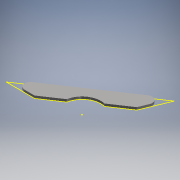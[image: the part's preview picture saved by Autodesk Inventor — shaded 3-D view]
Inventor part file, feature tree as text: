
AUTODESK INVENTOR PART (.ipt)
format: ipt  version: 2018 (Build 220112000, 112)  size: 124,928 bytes
history: native  units: in
note: dims shown in document units (in); Inventor stores cm internally (conversion verified against a paired STEP export)
features: sketch x2, extrude x1, fillet x1, projected_geometry x1
ambient origin geometry x8: Origin, YZ Plane, XZ Plane, XY Plane, X Axis, Y Axis, Z Axis, Center Point
bodies: Solid1 (feature_tree)
feature tree (5):
  extrude  "Extrusion1"  Depth=1.25in
  sketch  "Sketch2"  dims[d4=1.25in d5=1.5in d6=1.5in d7=0.7719in d8=0.125in d9=0.0in d10=0.5in d12=0.5in d13=1.0in d14=0.3in]
  fillet  "Fillet1"  Radius=1.25in
  sketch  "Sketch1"  dims[d0=0.7719in d2=1.56in d3=1.25in]
  projected_geometry  "Projected Loop1"
